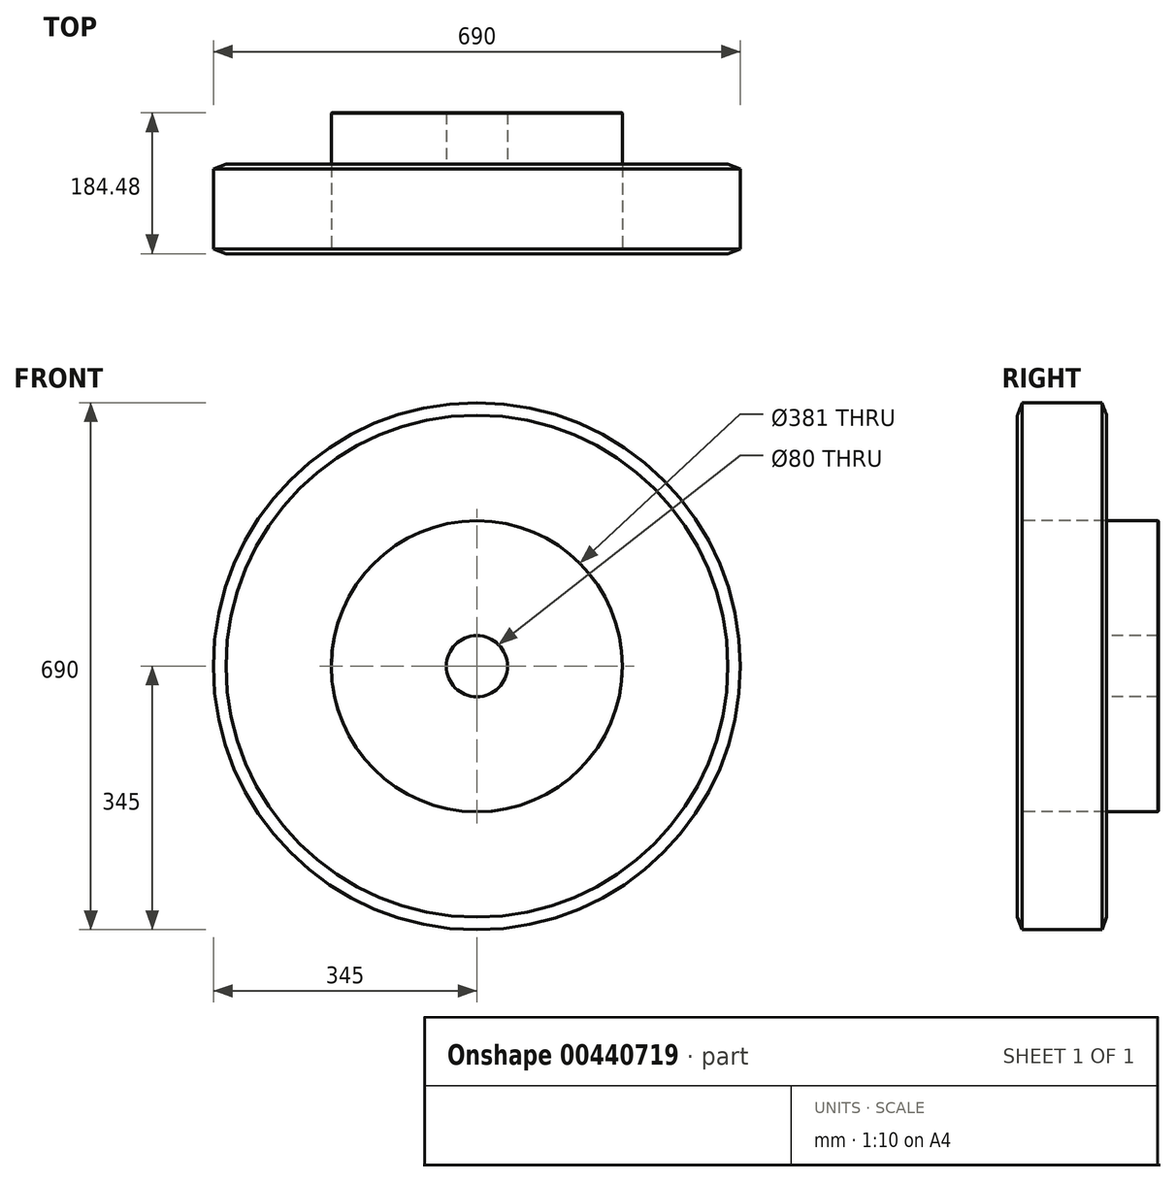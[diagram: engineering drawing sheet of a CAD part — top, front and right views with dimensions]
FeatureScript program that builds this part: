
annotation { "Feature Type Name" : "Feature", "Feature Type Description" : "" }
export const myFeature = defineFeature(function(context is Context, id is Id, definition is map)
    precondition{}
    {
        {
            var Q0;
            Q0=qCreatedBy(makeId("Right.planeOp"),FACE);
            var sketch = newSketch(context, id + "F0", { "sketchPlane" : qUnion([Q0])});
            skLineSegment(sketch, "E0", {"start": v(0, 0) * mm, "end": v(230.82, 0) * mm});
            skLineSegment(sketch, "E1.bottom", {"start": v(0, 345) * mm, "end": v(117, 345) * mm});
            skLineSegment(sketch, "E1.top", {"start": v(0, 40) * mm, "end": v(117, 40) * mm});
            skLineSegment(sketch, "E1.left", {"start": v(0, 345) * mm, "end": v(0, 40) * mm});
            skLineSegment(sketch, "E1.right", {"start": v(117, 345) * mm, "end": v(117, 40) * mm});
            skLineSegment(sketch, "E2.bottom", {"start": v(0, 40) * mm, "end": v(184.48, 40) * mm});
            skLineSegment(sketch, "E2.top", {"start": v(0, 190.5) * mm, "end": v(184.48, 190.5) * mm});
            skLineSegment(sketch, "E2.left", {"start": v(0, 40) * mm, "end": v(0, 190.5) * mm});
            skLineSegment(sketch, "E2.right", {"start": v(184.48, 40) * mm, "end": v(184.48, 190.5) * mm});
            skLineSegment(sketch, "E3.MirrorCS", {"start": v(0, -345) * mm, "end": v(117, -345) * mm});
            skLineSegment(sketch, "E4.MirrorCS", {"start": v(0, -40) * mm, "end": v(117, -40) * mm});
            skLineSegment(sketch, "E5.MirrorCS", {"start": v(0, -345) * mm, "end": v(0, -40) * mm});
            skLineSegment(sketch, "E6.MirrorCS", {"start": v(117, -345) * mm, "end": v(117, -40) * mm});
            skLineSegment(sketch, "E7.MirrorCS", {"start": v(184.48, -40) * mm, "end": v(184.48, -190.5) * mm});
            skLineSegment(sketch, "E8.MirrorCS", {"start": v(0, -40) * mm, "end": v(0, -190.5) * mm});
            skLineSegment(sketch, "E9.MirrorCS", {"start": v(0, -190.5) * mm, "end": v(184.48, -190.5) * mm});
            skLineSegment(sketch, "E10.MirrorCS", {"start": v(0, -40) * mm, "end": v(184.48, -40) * mm});
            skSolve(sketch);
        }
        {
            var Q0;
            {var subQ0=sQuery(id+"F0.wireOp",EDGE,"E1.bottom");Q0=makeQuery(id+"F0.imprint","IMPRINT",FACE,{"disambiguationData":[TD([[makeQuery(id+"F0.imprint","IMPRINT",EDGE,{"derivedFrom":subQ0}),-1.0]])]});}
            var Q1;
            {var subQ5=sQuery(id+"F0.wireOp",EDGE,"E2.left");Q1=makeQuery(id+"F0.imprint","IMPRINT",FACE,{"disambiguationData":[TD([[makeQuery(id+"F0.imprint","IMPRINT",EDGE,{"derivedFrom":subQ5}),-1.0]])]});}
            var Q2;
            {var subQ5=sQuery(id+"F0.wireOp",EDGE,"E2.right");Q2=makeQuery(id+"F0.imprint","IMPRINT",FACE,{"disambiguationData":[TD([[makeQuery(id+"F0.imprint","IMPRINT",EDGE,{"derivedFrom":subQ5}),1.0]])]});}
            var Q3;
            Q3=sQuery(id+"F0.wireOp",EDGE,"E0");
            revolve(context, id + "F1", {"entities" : qUnion([Q0, Q1, Q2]), "axis" : qUnion([Q3]), "revolveType" : RevolveType.FULL});
        }
        {
            var Q0;
            Q0=makeQuery(id+"F1.opRevolve","SWEPT_EDGE",EDGE,{"disambiguationData":[OSD([sQuery(id+"F0.wireOp",EDGE,"E1.right"),sQuery(id+"F0.wireOp",EDGE,"E2.top")])]});
            fillet(context, id + "F2", {"entities" : qUnion([Q0]), "radius" : 1.59 * mm, "tangentPropagation" : true, "allowEdgeOverflow" : false});
        }
        {
            var Q0;
            Q0=makeQuery(id+"F1.opRevolve","SWEPT_EDGE",EDGE,{"disambiguationData":[OSD([sQuery(id+"F0.wireOp",EDGE,"E2.top"),sQuery(id+"F0.wireOp",EDGE,"E2.right")])]});
            chamfer(context, id + "F3", {"entities" : qUnion([Q0]), "width" : 0.77 * mm, "tangentPropagation" : true});
        }
        {
            var Q0;
            {var subQ0=sQuery(id+"F0.wireOp",EDGE,"E1.right");Q0=makeQuery(id+"F2.opFillet","BLEND_EDGE",EDGE,{"blendedFrom":[makeQuery(id+"F1.opRevolve","SWEPT_EDGE",EDGE,{"disambiguationData":[OSD([subQ0,sQuery(id+"F0.wireOp",EDGE,"E2.top")])]}),makeQuery(id+"F1.opRevolve","SWEPT_FACE",FACE,{"disambiguationData":[OSD([subQ0])]})],"blendedInto":[makeQuery(id+"F1.opRevolve","SWEPT_FACE",FACE,{"disambiguationData":[OSD([subQ0])]})]});}
            var Q1;
            Q1=makeQuery(id+"F1.opRevolve","SWEPT_FACE",FACE,{"disambiguationData":[OSD([sQuery(id+"F0.wireOp",EDGE,"E1.bottom")])]});
            chamfer(context, id + "F4", {"entities" : qUnion([Q0, Q1]), "chamferType" : ChamferType.TWO_OFFSETS, "width1" : 6.35 * mm, "oppositeDirection" : false, "width2" : 16.5 * mm, "tangentPropagation" : true});
        }
    });
